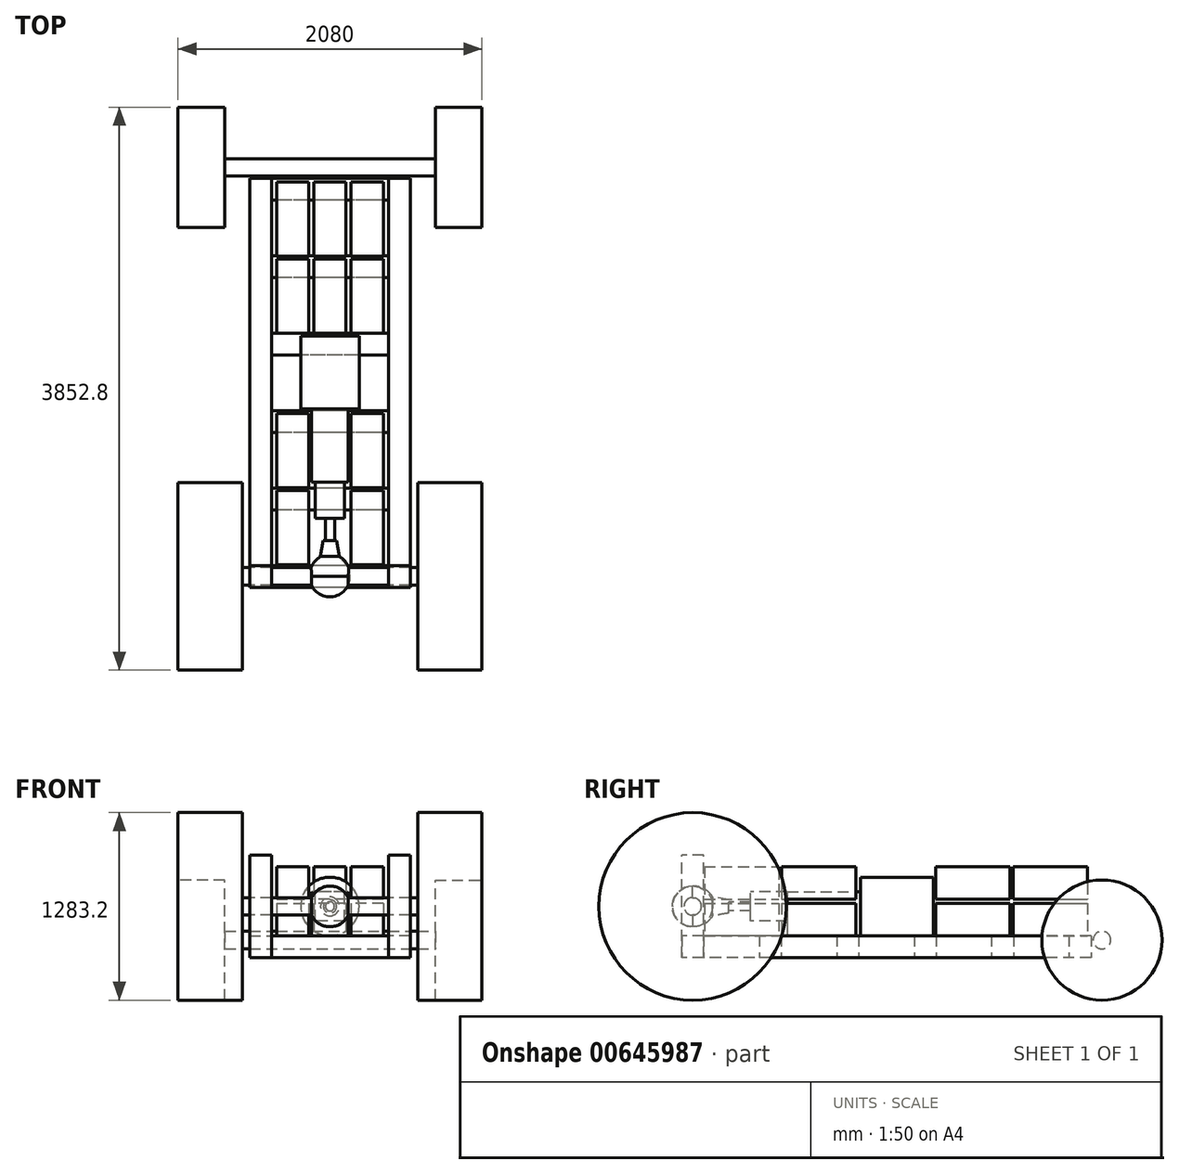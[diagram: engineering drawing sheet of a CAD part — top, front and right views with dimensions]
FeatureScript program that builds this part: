
annotation { "Feature Type Name" : "Feature", "Feature Type Description" : "" }
export const myFeature = defineFeature(function(context is Context, id is Id, definition is map)
    precondition{}
    {
        {
            var Q0;
            Q0=qCreatedBy(makeId("Right.planeOp"),FACE);
            var sketch = newSketch(context, id + "F0", { "sketchPlane" : qUnion([Q0])});
            skLineSegment(sketch, "E0", {"start": v(0, 0) * mm, "end": v(308.6, 0) * mm, "construction": true});
            skCircle(sketch, "E1", {"center": v(0, 0) * mm, "radius": 114.3 * mm, "construction": true});
            skLineSegment(sketch, "E2", {"start": v(246.64, 0) * mm, "end": v(246.64, 45.32) * mm});
            skLineSegment(sketch, "E3", {"start": v(246.64, 45.32) * mm, "end": v(136.12, 64.66) * mm});
            skArc(sketch, "E4", {"start": v(136.12, 64.66) * mm, "mid": v(78.24, 120.54) * mm, "end": v(0, 139.26) * mm});
            skLineSegment(sketch, "E5", {"start": v(0, 139.26) * mm, "end": v(0, 0) * mm});
            skLineSegment(sketch, "E6", {"start": v(0, 0) * mm, "end": v(246.64, 0) * mm});
            skLineSegment(sketch, "E7", {"start": v(0, 0) * mm, "end": v(-139.26, 0) * mm});
            skArc(sketch, "E8", {"start": v(0, 139.26) * mm, "mid": v(-98.59, 98.59) * mm, "end": v(-139.26, 0) * mm});
            skSolve(sketch);
        }
        {
            var Q0;
            Q0 = qSketchRegion(id + "F0", true);
            var Q1;
            Q1=sQuery(id+"F0.wireOp",EDGE,"E0");
            revolve(context, id + "F1", {"entities" : qUnion([Q0]), "axis" : qUnion([Q1]), "revolveType" : RevolveType.FULL});
        }
        {
            var Q0;
            Q0=qCreatedBy(makeId("Right.planeOp"),FACE);
            var sketch = newSketch(context, id + "F2", { "sketchPlane" : qUnion([Q0])});
            skCircle(sketch, "E9", {"center": v(0, 0) * mm, "radius": 60 * mm});
            skSolve(sketch);
        }
        {
            var Q0;
            Q0 = qSketchRegion(id + "F2", true);
            extrude(context, id + "F3", {"entities" : qUnion([Q0]), "operationType" : NewBodyOperationType.ADD, "endBound" : BoundingType.SYMMETRIC, "depth" : 1200 * mm, "offsetDistance" : 25 * mm});
        }
        {
            var Q0;
            Q0=qCreatedBy(makeId("Right.planeOp"),FACE);
            var sketch = newSketch(context, id + "F4", { "sketchPlane" : qUnion([Q0])});
            skLineSegment(sketch, "E10.bottom", {"start": v(646.64, -100) * mm, "end": v(396.64, -100) * mm});
            skLineSegment(sketch, "E10.top", {"start": v(646.64, 100) * mm, "end": v(396.64, 100) * mm});
            skLineSegment(sketch, "E10.left", {"start": v(646.64, -100) * mm, "end": v(646.64, 100) * mm});
            skLineSegment(sketch, "E10.right", {"start": v(396.64, -100) * mm, "end": v(396.64, 100) * mm});
            skPoint(sketch, "E10.middle", {"position": v(521.64, 0) * mm});
            skSolve(sketch);
        }
        {
            var Q0;
            Q0 = qSketchRegion(id + "F4", true);
            extrude(context, id + "F5", {"entities" : qUnion([Q0]), "endBound" : BoundingType.SYMMETRIC, "depth" : 200 * mm, "offsetDistance" : 25 * mm});
        }
        {
            var Q0;
            Q0=makeQuery(id+"F1.opRevolve","SWEPT_FACE",FACE,{"disambiguationData":[OSD([sQuery(id+"F0.wireOp",EDGE,"E2")])]});
            var sketch = newSketch(context, id + "F6", { "sketchPlane" : qUnion([Q0])});
            skCircle(sketch, "E11", {"center": v(0, 0) * mm, "radius": 31.09 * mm});
            skSolve(sketch);
        }
        {
            var Q0;
            Q0 = qSketchRegion(id + "F6", true);
            extrude(context, id + "F7", {"entities" : qUnion([Q0]), "endBound" : BoundingType.UP_TO_NEXT, "depth" : 25 * mm, "offsetDistance" : 25 * mm});
        }
        {
            var Q0;
            Q0=qCreatedBy(makeId("Right.planeOp"),FACE);
            var sketch = newSketch(context, id + "F8", { "sketchPlane" : qUnion([Q0])});
            skLineSegment(sketch, "E12.bottom", {"start": v(646.64, 100) * mm, "end": v(1146.64, 100) * mm});
            skLineSegment(sketch, "E12.top", {"start": v(646.64, -200) * mm, "end": v(1146.64, -200) * mm});
            skLineSegment(sketch, "E12.left", {"start": v(646.64, 100) * mm, "end": v(646.64, -200) * mm});
            skLineSegment(sketch, "E12.right", {"start": v(1146.64, 100) * mm, "end": v(1146.64, -200) * mm});
            skSolve(sketch);
        }
        {
            var Q0;
            Q0 = qSketchRegion(id + "F8", true);
            extrude(context, id + "F9", {"entities" : qUnion([Q0]), "endBound" : BoundingType.SYMMETRIC, "depth" : 250 * mm, "offsetDistance" : 25 * mm});
        }
        {
            var Q0;
            Q0=makeQuery(id+"F9.opExtrude","SWEPT_FACE",FACE,{"disambiguationData":[OSD([sQuery(id+"F8.wireOp",EDGE,"E12.right")])]});
            var sketch = newSketch(context, id + "F10", { "sketchPlane" : qUnion([Q0])});
            skCircle(sketch, "E13", {"center": v(0, 0) * mm, "radius": 200 * mm});
            skSolve(sketch);
        }
        {
            var Q0;
            Q0 = qSketchRegion(id + "F10", true);
            extrude(context, id + "F11", {"entities" : qUnion([Q0]), "depth" : 500 * mm, "offsetDistance" : 25 * mm});
        }
        {
            var Q0;
            Q0=makeQuery(id+"F3.opExtrude","CAP_FACE",FACE,{"disambiguationData":[OSD([sQuery(id+"F2.wireOp",EDGE,"E9")])],"isStart":false});
            var sketch = newSketch(context, id + "F12", { "sketchPlane" : qUnion([Q0])});
            skCircle(sketch, "E14", {"center": v(0, 0) * mm, "radius": 641.6 * mm});
            skSolve(sketch);
        }
        {
            var Q0;
            Q0 = qSketchRegion(id + "F12", true);
            extrude(context, id + "F13", {"entities" : qUnion([Q0]), "depth" : 440 * mm, "offsetDistance" : 25 * mm});
        }
        {
            var Q0;
            Q0=makeQuery(id+"F13.opExtrude","SWEPT_BODY",BODY,{"disambiguationData":[OSD([sQuery(id+"F12.wireOp",EDGE,"E14")])]});
            var Q1;
            Q1=qCreatedBy(makeId("Right.planeOp"),FACE);
            mirror(context, id + "F14", {"entities" : qUnion([Q0]), "mirrorPlane" : qUnion([Q1])});
        }
        {
            var Q0;
            Q0=makeQuery(id+"F9.opExtrude","SWEPT_FACE",FACE,{"disambiguationData":[OSD([sQuery(id+"F8.wireOp",EDGE,"E12.top")])]});
            var sketch = newSketch(context, id + "F15", { "sketchPlane" : qUnion([Q0])});
            skLineSegment(sketch, "E15.bottom", {"start": v(365, -80) * mm, "end": v(145, -80) * mm});
            skLineSegment(sketch, "E15.top", {"start": v(365, -588) * mm, "end": v(145, -588) * mm});
            skLineSegment(sketch, "E15.left", {"start": v(365, -80) * mm, "end": v(365, -588) * mm});
            skLineSegment(sketch, "E15.right", {"start": v(145, -80) * mm, "end": v(145, -588) * mm});
            skLineSegment(sketch, "E16.bottom", {"start": v(365, -608) * mm, "end": v(145, -608) * mm});
            skLineSegment(sketch, "E16.top", {"start": v(365, -1116) * mm, "end": v(145, -1116) * mm});
            skLineSegment(sketch, "E16.left", {"start": v(365, -608) * mm, "end": v(365, -1116) * mm});
            skLineSegment(sketch, "E16.right", {"start": v(145, -608) * mm, "end": v(145, -1116) * mm});
            skLineSegment(sketch, "E17.top", {"start": v(365, -2172) * mm, "end": v(145, -2172) * mm});
            skLineSegment(sketch, "E17.left", {"start": v(365, -1664) * mm, "end": v(365, -2172) * mm});
            skLineSegment(sketch, "E17.right", {"start": v(145, -1664) * mm, "end": v(145, -2172) * mm});
            skLineSegment(sketch, "E18.bottom", {"start": v(110, -1664) * mm, "end": v(-110, -1664) * mm});
            skLineSegment(sketch, "E18.top", {"start": v(110, -2172) * mm, "end": v(-110, -2172) * mm});
            skLineSegment(sketch, "E18.left", {"start": v(110, -1664) * mm, "end": v(110, -2172) * mm});
            skLineSegment(sketch, "E18.right", {"start": v(-110, -1664) * mm, "end": v(-110, -2172) * mm});
            skLineSegment(sketch, "E19", {"start": v(0, 0) * mm, "end": v(0, -2805.08) * mm, "construction": true});
            skLineSegment(sketch, "E20.bottom", {"start": v(365, -2192) * mm, "end": v(145, -2192) * mm});
            skLineSegment(sketch, "E20.top", {"start": v(365, -2700) * mm, "end": v(145, -2700) * mm});
            skLineSegment(sketch, "E20.left", {"start": v(365, -2192) * mm, "end": v(365, -2700) * mm});
            skLineSegment(sketch, "E20.right", {"start": v(145, -2192) * mm, "end": v(145, -2700) * mm});
            skPoint(sketch, "E21.oppositeSnap0", {"position": v(255, -2700) * mm});
            skLineSegment(sketch, "E21.bottom", {"start": v(110, -2192) * mm, "end": v(-110, -2192) * mm});
            skLineSegment(sketch, "E21.top", {"start": v(110, -2700) * mm, "end": v(-110, -2700) * mm});
            skLineSegment(sketch, "E21.left", {"start": v(110, -2192) * mm, "end": v(110, -2700) * mm});
            skLineSegment(sketch, "E21.right", {"start": v(-110, -2192) * mm, "end": v(-110, -2700) * mm});
            skLineSegment(sketch, "E22", {"start": v(365, -1664) * mm, "end": v(145, -1664) * mm});
            skSolve(sketch);
        }
        {
            var Q0;
            Q0 = qSketchRegion(id + "F15", true);
            extrude(context, id + "F16", {"entities" : qUnion([Q0]), "oppositeDirection" : true, "depth" : 220 * mm, "offsetDistance" : 25 * mm});
        }
        {
            var Q0;
            Q0=makeQuery(id+"F16.opExtrude","SWEPT_BODY",BODY,{"disambiguationData":[OSD([sQuery(id+"F15.wireOp",EDGE,"E17.bottom"),sQuery(id+"F15.wireOp",EDGE,"E17.top"),sQuery(id+"F15.wireOp",EDGE,"E17.left"),sQuery(id+"F15.wireOp",EDGE,"E17.right")])]});
            var Q1;
            Q1=makeQuery(id+"F16.opExtrude","SWEPT_BODY",BODY,{"disambiguationData":[OSD([sQuery(id+"F15.wireOp",EDGE,"uiYWyO02-muJb-upMI-98Jg-HfNWmcqVRrhf.bottom"),sQuery(id+"F15.wireOp",EDGE,"uiYWyO02-muJb-upMI-98Jg-HfNWmcqVRrhf.top"),sQuery(id+"F15.wireOp",EDGE,"uiYWyO02-muJb-upMI-98Jg-HfNWmcqVRrhf.left"),sQuery(id+"F15.wireOp",EDGE,"uiYWyO02-muJb-upMI-98Jg-HfNWmcqVRrhf.right")])]});
            var Q2;
            Q2=makeQuery(id+"F16.opExtrude","SWEPT_BODY",BODY,{"disambiguationData":[OSD([sQuery(id+"F15.wireOp",EDGE,"E16.bottom"),sQuery(id+"F15.wireOp",EDGE,"E16.top"),sQuery(id+"F15.wireOp",EDGE,"E16.left"),sQuery(id+"F15.wireOp",EDGE,"E16.right")])]});
            var Q3;
            Q3=makeQuery(id+"F16.opExtrude","SWEPT_BODY",BODY,{"disambiguationData":[OSD([sQuery(id+"F15.wireOp",EDGE,"E15.bottom"),sQuery(id+"F15.wireOp",EDGE,"E15.top"),sQuery(id+"F15.wireOp",EDGE,"E15.left"),sQuery(id+"F15.wireOp",EDGE,"E15.right")])]});
            var Q4;
            Q4=makeQuery(id+"F16.opExtrude","SWEPT_BODY",BODY,{"disambiguationData":[OSD([sQuery(id+"F15.wireOp",EDGE,"E20.bottom"),sQuery(id+"F15.wireOp",EDGE,"E20.top"),sQuery(id+"F15.wireOp",EDGE,"E20.left"),sQuery(id+"F15.wireOp",EDGE,"E20.right")])]});
            var Q5;
            Q5=qCreatedBy(makeId("Right.planeOp"),FACE);
            mirror(context, id + "F17", {"entities" : qUnion([Q0, Q1, Q2, Q3, Q4]), "mirrorPlane" : qUnion([Q5])});
        }
        {
            var Q0;
            Q0=qCreatedBy(makeId("Top.planeOp"),FACE);
            var sketch = newSketch(context, id + "F18", { "sketchPlane" : qUnion([Q0])});
            skLineSegment(sketch, "E23", {"start": v(624.6, 2800) * mm, "end": v(-972.52, 2800) * mm, "construction": true});
            skSolve(sketch);
        }
        {
            var Q0;
            Q0=makeQuery(id+"F16.opExtrude","SWEPT_BODY",BODY,{"disambiguationData":[OSD([sQuery(id+"F15.wireOp",EDGE,"E15.bottom"),sQuery(id+"F15.wireOp",EDGE,"E15.top"),sQuery(id+"F15.wireOp",EDGE,"E15.left"),sQuery(id+"F15.wireOp",EDGE,"E15.right")])]});
            var Q1;
            Q1=makeQuery(id+"F16.opExtrude","SWEPT_BODY",BODY,{"disambiguationData":[OSD([sQuery(id+"F15.wireOp",EDGE,"E16.bottom"),sQuery(id+"F15.wireOp",EDGE,"E16.top"),sQuery(id+"F15.wireOp",EDGE,"E16.left"),sQuery(id+"F15.wireOp",EDGE,"E16.right")])]});
            var Q2;
            Q2=makeQuery(id+"F16.opExtrude","SWEPT_BODY",BODY,{"disambiguationData":[OSD([sQuery(id+"F15.wireOp",EDGE,"uiYWyO02-muJb-upMI-98Jg-HfNWmcqVRrhf.bottom"),sQuery(id+"F15.wireOp",EDGE,"uiYWyO02-muJb-upMI-98Jg-HfNWmcqVRrhf.top"),sQuery(id+"F15.wireOp",EDGE,"uiYWyO02-muJb-upMI-98Jg-HfNWmcqVRrhf.left"),sQuery(id+"F15.wireOp",EDGE,"uiYWyO02-muJb-upMI-98Jg-HfNWmcqVRrhf.right")])]});
            var Q3;
            Q3=makeQuery(id+"F16.opExtrude","SWEPT_BODY",BODY,{"disambiguationData":[OSD([sQuery(id+"F15.wireOp",EDGE,"E17.bottom"),sQuery(id+"F15.wireOp",EDGE,"E17.top"),sQuery(id+"F15.wireOp",EDGE,"E17.left"),sQuery(id+"F15.wireOp",EDGE,"E17.right")])]});
            var Q4;
            Q4=makeQuery(id+"F16.opExtrude","SWEPT_BODY",BODY,{"disambiguationData":[OSD([sQuery(id+"F15.wireOp",EDGE,"E20.bottom"),sQuery(id+"F15.wireOp",EDGE,"E20.top"),sQuery(id+"F15.wireOp",EDGE,"E20.left"),sQuery(id+"F15.wireOp",EDGE,"E20.right")])]});
            var Q5;
            Q5=makeQuery(id+"F16.opExtrude","SWEPT_BODY",BODY,{"disambiguationData":[OSD([sQuery(id+"F15.wireOp",EDGE,"E21.bottom"),sQuery(id+"F15.wireOp",EDGE,"E21.top"),sQuery(id+"F15.wireOp",EDGE,"E21.left"),sQuery(id+"F15.wireOp",EDGE,"E21.right")])]});
            var Q6;
            Q6=makeQuery(id+"F16.opExtrude","SWEPT_BODY",BODY,{"disambiguationData":[OSD([sQuery(id+"F15.wireOp",EDGE,"E18.bottom"),sQuery(id+"F15.wireOp",EDGE,"E18.top"),sQuery(id+"F15.wireOp",EDGE,"E18.left"),sQuery(id+"F15.wireOp",EDGE,"E18.right")])]});
            var Q7;
            Q7=makeQuery(id+"F17.opPattern","COPY",BODY,{"derivedFrom":makeQuery(id+"F16.opExtrude","SWEPT_BODY",BODY,{"disambiguationData":[OSD([sQuery(id+"F15.wireOp",EDGE,"E20.bottom"),sQuery(id+"F15.wireOp",EDGE,"E20.top"),sQuery(id+"F15.wireOp",EDGE,"E20.left"),sQuery(id+"F15.wireOp",EDGE,"E20.right")])]}),"instanceName":"1"});
            var Q8;
            Q8=makeQuery(id+"F17.opPattern","COPY",BODY,{"derivedFrom":makeQuery(id+"F16.opExtrude","SWEPT_BODY",BODY,{"disambiguationData":[OSD([sQuery(id+"F15.wireOp",EDGE,"E17.bottom"),sQuery(id+"F15.wireOp",EDGE,"E17.top"),sQuery(id+"F15.wireOp",EDGE,"E17.left"),sQuery(id+"F15.wireOp",EDGE,"E17.right")])]}),"instanceName":"1"});
            var Q9;
            Q9=makeQuery(id+"F17.opPattern","COPY",BODY,{"derivedFrom":makeQuery(id+"F16.opExtrude","SWEPT_BODY",BODY,{"disambiguationData":[OSD([sQuery(id+"F15.wireOp",EDGE,"uiYWyO02-muJb-upMI-98Jg-HfNWmcqVRrhf.bottom"),sQuery(id+"F15.wireOp",EDGE,"uiYWyO02-muJb-upMI-98Jg-HfNWmcqVRrhf.top"),sQuery(id+"F15.wireOp",EDGE,"uiYWyO02-muJb-upMI-98Jg-HfNWmcqVRrhf.left"),sQuery(id+"F15.wireOp",EDGE,"uiYWyO02-muJb-upMI-98Jg-HfNWmcqVRrhf.right")])]}),"instanceName":"1"});
            var Q10;
            Q10=makeQuery(id+"F17.opPattern","COPY",BODY,{"derivedFrom":makeQuery(id+"F16.opExtrude","SWEPT_BODY",BODY,{"disambiguationData":[OSD([sQuery(id+"F15.wireOp",EDGE,"E16.bottom"),sQuery(id+"F15.wireOp",EDGE,"E16.top"),sQuery(id+"F15.wireOp",EDGE,"E16.left"),sQuery(id+"F15.wireOp",EDGE,"E16.right")])]}),"instanceName":"1"});
            var Q11;
            Q11=makeQuery(id+"F17.opPattern","COPY",BODY,{"derivedFrom":makeQuery(id+"F16.opExtrude","SWEPT_BODY",BODY,{"disambiguationData":[OSD([sQuery(id+"F15.wireOp",EDGE,"E15.bottom"),sQuery(id+"F15.wireOp",EDGE,"E15.top"),sQuery(id+"F15.wireOp",EDGE,"E15.left"),sQuery(id+"F15.wireOp",EDGE,"E15.right")])]}),"instanceName":"1"});
            var Q12;
            Q12=makeQuery(id+"F16.opExtrude","SWEPT_EDGE",EDGE,{"disambiguationData":[OSD([sQuery(id+"F15.wireOp",EDGE,"E20.top"),sQuery(id+"F15.wireOp",EDGE,"E20.left")])]});
            transform(context, id + "F19", {"entities" : qUnion([Q0, Q1, Q2, Q3, Q4, Q5, Q6, Q7, Q8, Q9, Q10, Q11]), "transformType" : TransformType.TRANSLATION_DISTANCE, "transformDirection" : qUnion([Q12]), "distance" : 250 * mm, "oppositeDirection" : true, "makeCopy" : true});
        }
        {
            var Q0;
            Q0=makeQuery(id+"F13.opExtrude","CAP_FACE",FACE,{"disambiguationData":[OSD([sQuery(id+"F12.wireOp",EDGE,"E14")])],"isStart":false});
            var sketch = newSketch(context, id + "F20", { "sketchPlane" : qUnion([Q0])});
            skLineSegment(sketch, "E24", {"start": v(268.16, -641.6) * mm, "end": v(-4055.37, -641.6) * mm, "construction": true});
            skCircle(sketch, "E25", {"center": v(2800, -230.4) * mm, "radius": 411.2 * mm});
            skSolve(sketch);
        }
        {
            var Q0;
            Q0 = qSketchRegion(id + "F20", true);
            extrude(context, id + "F21", {"entities" : qUnion([Q0]), "oppositeDirection" : true, "depth" : 320 * mm, "offsetDistance" : 25 * mm});
        }
        {
            var Q0;
            Q0=makeQuery(id+"F21.opExtrude","SWEPT_BODY",BODY,{"disambiguationData":[OSD([sQuery(id+"F20.wireOp",EDGE,"E25")])]});
            var Q1;
            Q1=qCreatedBy(makeId("Right.planeOp"),FACE);
            mirror(context, id + "F22", {"entities" : qUnion([Q0]), "mirrorPlane" : qUnion([Q1])});
        }
        {
            var Q0;
            Q0=qCreatedBy(makeId("Right.planeOp"),FACE);
            cPlane(context, id + "F23", {"entities" : qUnion([Q0]), "cplaneType" : CPlaneType.OFFSET, "offset" : 400 * mm, "width" : 150 * mm, "height" : 150 * mm});
        }
        {
            var Q0;
            Q0=qCreatedBy(id+"F23.planeOp",FACE);
            var sketch = newSketch(context, id + "F24", { "sketchPlane" : qUnion([Q0])});
            skLineSegment(sketch, "E26.bottom", {"start": v(75, -350) * mm, "end": v(-75, -350) * mm});
            skLineSegment(sketch, "E26.top", {"start": v(75, 350) * mm, "end": v(-75, 350) * mm});
            skLineSegment(sketch, "E26.left", {"start": v(75, -350) * mm, "end": v(75, 350) * mm});
            skLineSegment(sketch, "E26.right", {"start": v(-75, -350) * mm, "end": v(-75, 350) * mm});
            skPoint(sketch, "E26.middle", {"position": v(0, 0) * mm});
            skSolve(sketch);
        }
        {
            var Q0;
            Q0 = qSketchRegion(id + "F24", true);
            extrude(context, id + "F25", {"entities" : qUnion([Q0]), "depth" : 150 * mm, "offsetDistance" : 25 * mm});
        }
        {
            var Q0;
            Q0=makeQuery(id+"F25.opExtrude","SWEPT_FACE",FACE,{"disambiguationData":[OSD([sQuery(id+"F24.wireOp",EDGE,"E26.left")])]});
            var sketch = newSketch(context, id + "F26", { "sketchPlane" : qUnion([Q0])});
            skLineSegment(sketch, "E27.bottom", {"start": v(-550, -350) * mm, "end": v(-400, -350) * mm});
            skLineSegment(sketch, "E27.top", {"start": v(-550, -200) * mm, "end": v(-400, -200) * mm});
            skLineSegment(sketch, "E27.left", {"start": v(-550, -350) * mm, "end": v(-550, -200) * mm});
            skLineSegment(sketch, "E27.right", {"start": v(-400, -350) * mm, "end": v(-400, -200) * mm});
            skSolve(sketch);
        }
        {
            var Q0;
            Q0 = qSketchRegion(id + "F26", true);
            extrude(context, id + "F27", {"entities" : qUnion([Q0]), "depth" : (2800 - 150) * mm, "offsetDistance" : 25 * mm});
        }
        {
            var Q0;
            Q0=makeQuery(id+"F21.opExtrude","CAP_FACE",FACE,{"disambiguationData":[OSD([sQuery(id+"F20.wireOp",EDGE,"E25")])],"isStart":false});
            var sketch = newSketch(context, id + "F28", { "sketchPlane" : qUnion([Q0])});
            skCircle(sketch, "E28", {"center": v(-2800, -230.4) * mm, "radius": 60 * mm});
            skSolve(sketch);
        }
        {
            var Q0;
            Q0 = qSketchRegion(id + "F28", true);
            extrude(context, id + "F29", {"entities" : qUnion([Q0]), "endBound" : BoundingType.UP_TO_NEXT, "depth" : 25 * mm, "offsetDistance" : 25 * mm});
        }
        {
            var Q0;
            Q0=makeQuery(id+"F25.opExtrude","SWEPT_BODY",BODY,{"disambiguationData":[OSD([sQuery(id+"F24.wireOp",EDGE,"E26.bottom"),sQuery(id+"F24.wireOp",EDGE,"E26.top"),sQuery(id+"F24.wireOp",EDGE,"E26.left"),sQuery(id+"F24.wireOp",EDGE,"E26.right")])]});
            var Q1;
            Q1=makeQuery(id+"F27.opExtrude","SWEPT_BODY",BODY,{"disambiguationData":[OSD([sQuery(id+"F26.wireOp",EDGE,"E27.bottom"),sQuery(id+"F26.wireOp",EDGE,"E27.top"),sQuery(id+"F26.wireOp",EDGE,"E27.left"),sQuery(id+"F26.wireOp",EDGE,"E27.right")])]});
            var Q2;
            Q2=qCreatedBy(makeId("Right.planeOp"),FACE);
            mirror(context, id + "F30", {"entities" : qUnion([Q0, Q1]), "mirrorPlane" : qUnion([Q2])});
        }
        {
            var Q0;
            Q0=makeQuery(id+"F27.opExtrude","SWEPT_FACE",FACE,{"disambiguationData":[OSD([sQuery(id+"F26.wireOp",EDGE,"E27.bottom")])]});
            var sketch = newSketch(context, id + "F31", { "sketchPlane" : qUnion([Q0])});
            skLineSegment(sketch, "E29.bottom", {"start": v(400, -605) * mm, "end": v(-400, -605) * mm});
            skLineSegment(sketch, "E29.top", {"start": v(400, -455) * mm, "end": v(-400, -455) * mm});
            skLineSegment(sketch, "E29.left", {"start": v(400, -605) * mm, "end": v(400, -455) * mm});
            skLineSegment(sketch, "E29.right", {"start": v(-400, -605) * mm, "end": v(-400, -455) * mm});
            skLineSegment(sketch, "E30.bottom", {"start": v(400, -1135) * mm, "end": v(-400, -1135) * mm});
            skLineSegment(sketch, "E30.top", {"start": v(400, -985) * mm, "end": v(-400, -985) * mm});
            skLineSegment(sketch, "E30.left", {"start": v(400, -1135) * mm, "end": v(400, -985) * mm});
            skLineSegment(sketch, "E30.right", {"start": v(-400, -1135) * mm, "end": v(-400, -985) * mm});
            skLineSegment(sketch, "E31.bottom", {"start": v(400, -1665) * mm, "end": v(-400, -1665) * mm});
            skLineSegment(sketch, "E31.top", {"start": v(400, -1515) * mm, "end": v(-400, -1515) * mm});
            skLineSegment(sketch, "E31.left", {"start": v(400, -1665) * mm, "end": v(400, -1515) * mm});
            skLineSegment(sketch, "E31.right", {"start": v(-400, -1665) * mm, "end": v(-400, -1515) * mm});
            skLineSegment(sketch, "E32.bottom", {"start": v(400, -2725) * mm, "end": v(-400, -2725) * mm});
            skLineSegment(sketch, "E32.top", {"start": v(400, -2575) * mm, "end": v(-400, -2575) * mm});
            skLineSegment(sketch, "E32.left", {"start": v(400, -2725) * mm, "end": v(400, -2575) * mm});
            skLineSegment(sketch, "E32.right", {"start": v(-400, -2725) * mm, "end": v(-400, -2575) * mm});
            skLineSegment(sketch, "E33.bottom", {"start": v(400, -2195) * mm, "end": v(-400, -2195) * mm});
            skLineSegment(sketch, "E33.top", {"start": v(400, -2045) * mm, "end": v(-400, -2045) * mm});
            skLineSegment(sketch, "E33.left", {"start": v(400, -2195) * mm, "end": v(400, -2045) * mm});
            skLineSegment(sketch, "E33.right", {"start": v(-400, -2195) * mm, "end": v(-400, -2045) * mm});
            skLineSegment(sketch, "E34.bottom", {"start": v(400, -75) * mm, "end": v(-400, -75) * mm});
            skLineSegment(sketch, "E34.top", {"start": v(400, 75) * mm, "end": v(-400, 75) * mm});
            skLineSegment(sketch, "E34.left", {"start": v(400, -75) * mm, "end": v(400, 75) * mm});
            skLineSegment(sketch, "E34.right", {"start": v(-400, -75) * mm, "end": v(-400, 75) * mm});
            skLineSegment(sketch, "E35", {"start": v(281.53, -75) * mm, "end": v(281.53, -455) * mm, "construction": true});
            skLineSegment(sketch, "E36", {"start": v(-218.36, -605) * mm, "end": v(-218.36, -985) * mm, "construction": true});
            skLineSegment(sketch, "E37", {"start": v(293.83, -1135) * mm, "end": v(293.83, -1515) * mm, "construction": true});
            skLineSegment(sketch, "E38", {"start": v(-303.84, -1665) * mm, "end": v(-303.84, -2045) * mm, "construction": true});
            skLineSegment(sketch, "E39", {"start": v(293.83, -2195) * mm, "end": v(293.83, -2575) * mm, "construction": true});
            skSolve(sketch);
        }
        {
            var Q0;
            Q0 = qSketchRegion(id + "F31", true);
            extrude(context, id + "F32", {"entities" : qUnion([Q0]), "oppositeDirection" : true, "depth" : 150 * mm, "offsetDistance" : 25 * mm});
        }
    });
